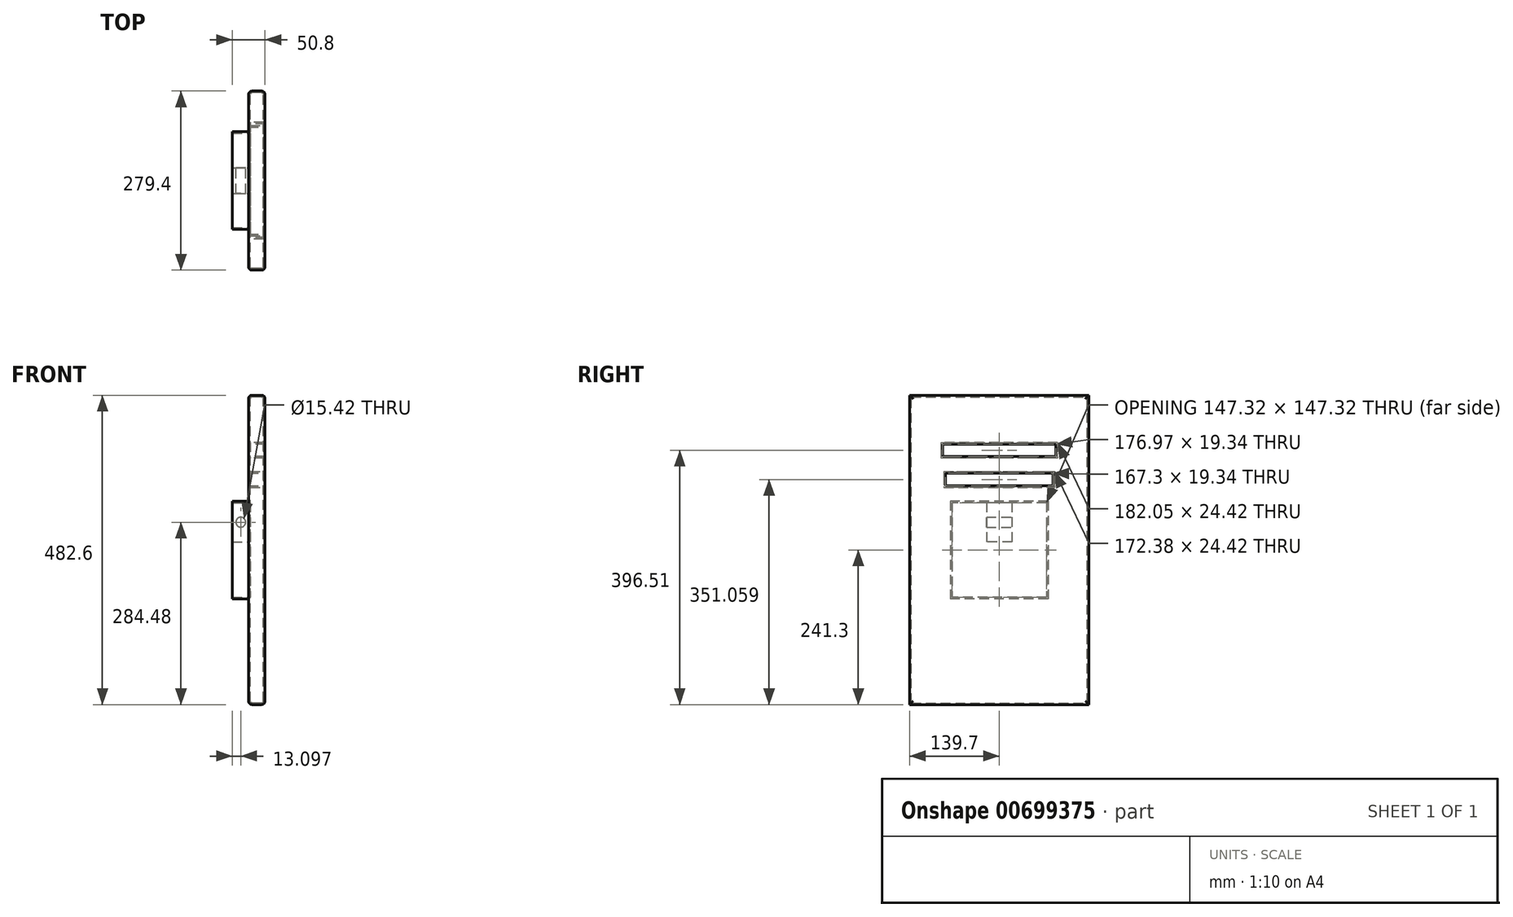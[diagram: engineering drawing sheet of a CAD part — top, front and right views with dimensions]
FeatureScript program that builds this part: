
annotation { "Feature Type Name" : "Feature", "Feature Type Description" : "" }
export const myFeature = defineFeature(function(context is Context, id is Id, definition is map)
    precondition{}
    {
        {
            var Q0;
            Q0=qCreatedBy(makeId("Right.planeOp"),FACE);
            var sketch = newSketch(context, id + "F0", { "sketchPlane" : qUnion([Q0])});
            skLineSegment(sketch, "E0.bottom", {"start": v(139.7, 241.3) * mm, "end": v(-139.7, 241.3) * mm});
            skLineSegment(sketch, "E0.top", {"start": v(139.7, -241.3) * mm, "end": v(-139.7, -241.3) * mm});
            skLineSegment(sketch, "E0.left", {"start": v(139.7, 241.3) * mm, "end": v(139.7, -241.3) * mm});
            skLineSegment(sketch, "E0.right", {"start": v(-139.7, 241.3) * mm, "end": v(-139.7, -241.3) * mm});
            skPoint(sketch, "E0.middle", {"position": v(0, 0) * mm});
            skSolve(sketch);
        }
        {
            var Q0;
            Q0 = qSketchRegion(id + "F0", true);
            var Q1;
            Q1=makeQuery(id+"F0.imprint","IMPRINT",FACE,{"disambiguationData":[TD([[makeQuery(id+"F0.imprint","IMPRINT",EDGE,{"derivedFrom":sQuery(id+"F0.wireOp",EDGE,"E0.bottom")}),1.0]])]});
            extrude(context, id + "F1", {"entities" : qUnion([Q0, Q1]), "depth" : 25.4 * mm, "offsetDistance" : 25.4 * mm});
        }
        {
            var Q0;
            Q0=makeQuery(id+"F1.opExtrude","CAP_FACE",FACE,{"disambiguationData":[OSD([sQuery(id+"F0.wireOp",EDGE,"E0.bottom"),sQuery(id+"F0.wireOp",EDGE,"E0.top"),sQuery(id+"F0.wireOp",EDGE,"E0.left"),sQuery(id+"F0.wireOp",EDGE,"E0.right")])],"isStart":true});
            fillet(context, id + "F2", {"entities" : qUnion([Q0]), "radius" : 5.08 * mm, "tangentPropagation" : true, "allowEdgeOverflow" : false});
        }
        {
            var Q0;
            Q0=makeQuery(id+"F1.opExtrude","CAP_FACE",FACE,{"disambiguationData":[OSD([sQuery(id+"F0.wireOp",EDGE,"E0.bottom"),sQuery(id+"F0.wireOp",EDGE,"E0.top"),sQuery(id+"F0.wireOp",EDGE,"E0.left"),sQuery(id+"F0.wireOp",EDGE,"E0.right")])],"isStart":false});
            fillet(context, id + "F3", {"entities" : qUnion([Q0]), "radius" : 5.08 * mm, "tangentPropagation" : true, "allowEdgeOverflow" : false});
        }
        {
            var Q0;
            Q0=makeQuery(id+"F1.opExtrude","CAP_FACE",FACE,{"disambiguationData":[OSD([sQuery(id+"F0.wireOp",EDGE,"E0.bottom"),sQuery(id+"F0.wireOp",EDGE,"E0.top"),sQuery(id+"F0.wireOp",EDGE,"E0.left"),sQuery(id+"F0.wireOp",EDGE,"E0.right")])],"isStart":true});
            var sketch = newSketch(context, id + "F4", { "sketchPlane" : qUnion([Q0])});
            skLineSegment(sketch, "E1.bottom", {"start": v(-88.48, 164.88) * mm, "end": v(88.48, 164.88) * mm});
            skLineSegment(sketch, "E1.top", {"start": v(-88.48, 145.54) * mm, "end": v(88.48, 145.54) * mm});
            skLineSegment(sketch, "E1.left", {"start": v(-88.48, 164.88) * mm, "end": v(-88.48, 145.54) * mm});
            skLineSegment(sketch, "E1.right", {"start": v(88.48, 164.88) * mm, "end": v(88.48, 145.54) * mm});
            skPoint(sketch, "E1.middle", {"position": v(0, 155.21) * mm});
            skSolve(sketch);
        }
        {
            var Q0;
            Q0=makeQuery(id+"F4.imprint","IMPRINT",FACE,{"disambiguationData":[TD([[makeQuery(id+"F4.imprint","IMPRINT",EDGE,{"derivedFrom":sQuery(id+"F4.wireOp",EDGE,"E1.bottom")}),-1.0]])]});
            extrude(context, id + "F5", {"entities" : qUnion([Q0]), "operationType" : NewBodyOperationType.REMOVE, "oppositeDirection" : true, "depth" : 25.4 * mm, "offsetDistance" : 25.4 * mm});
        }
        {
            var Q0;
            Q0=makeQuery(id+"F1.opExtrude","CAP_FACE",FACE,{"disambiguationData":[OSD([sQuery(id+"F0.wireOp",EDGE,"E0.bottom"),sQuery(id+"F0.wireOp",EDGE,"E0.top"),sQuery(id+"F0.wireOp",EDGE,"E0.left"),sQuery(id+"F0.wireOp",EDGE,"E0.right")])],"isStart":false});
            var sketch = newSketch(context, id + "F6", { "sketchPlane" : qUnion([Q0])});
            skLineSegment(sketch, "E2.bottom", {"start": v(-83.65, 119.43) * mm, "end": v(83.65, 119.43) * mm});
            skLineSegment(sketch, "E2.top", {"start": v(-83.65, 100.09) * mm, "end": v(83.65, 100.09) * mm});
            skLineSegment(sketch, "E2.left", {"start": v(-83.65, 119.43) * mm, "end": v(-83.65, 100.09) * mm});
            skLineSegment(sketch, "E2.right", {"start": v(83.65, 119.43) * mm, "end": v(83.65, 100.09) * mm});
            skPoint(sketch, "E2.middle", {"position": v(0, 109.76) * mm});
            skSolve(sketch);
        }
        {
            var Q0;
            Q0=makeQuery(id+"F6.imprint","IMPRINT",FACE,{"disambiguationData":[TD([[makeQuery(id+"F6.imprint","IMPRINT",EDGE,{"derivedFrom":sQuery(id+"F6.wireOp",EDGE,"E2.bottom")}),-1.0]])]});
            extrude(context, id + "F7", {"entities" : qUnion([Q0]), "operationType" : NewBodyOperationType.REMOVE, "oppositeDirection" : true, "depth" : 25.4 * mm, "offsetDistance" : 25.4 * mm});
        }
        {
            var Q0;
            Q0=makeQuery(id+"F1.opExtrude","CAP_FACE",FACE,{"disambiguationData":[OSD([sQuery(id+"F0.wireOp",EDGE,"E0.bottom"),sQuery(id+"F0.wireOp",EDGE,"E0.top"),sQuery(id+"F0.wireOp",EDGE,"E0.left"),sQuery(id+"F0.wireOp",EDGE,"E0.right")])],"isStart":true});
            var sketch = newSketch(context, id + "F8", { "sketchPlane" : qUnion([Q0])});
            skLineSegment(sketch, "E3.bottom", {"start": v(-76.2, 76.2) * mm, "end": v(76.2, 76.2) * mm});
            skLineSegment(sketch, "E3.top", {"start": v(-76.2, -76.2) * mm, "end": v(76.2, -76.2) * mm});
            skLineSegment(sketch, "E3.left", {"start": v(-76.2, 76.2) * mm, "end": v(-76.2, -76.2) * mm});
            skLineSegment(sketch, "E3.right", {"start": v(76.2, 76.2) * mm, "end": v(76.2, -76.2) * mm});
            skPoint(sketch, "E3.middle", {"position": v(0, 0) * mm});
            skSolve(sketch);
        }
        {
            var Q0;
            Q0=makeQuery(id+"F8.imprint","IMPRINT",FACE,{"disambiguationData":[TD([[makeQuery(id+"F8.imprint","IMPRINT",EDGE,{"derivedFrom":sQuery(id+"F8.wireOp",EDGE,"E3.bottom")}),-1.0]])]});
            extrude(context, id + "F9", {"entities" : qUnion([Q0]), "operationType" : NewBodyOperationType.ADD, "depth" : 25.4 * mm, "offsetDistance" : 25.4 * mm});
        }
        {
            var Q0;
            Q0=makeQuery(id+"F9.opExtrude","CAP_FACE",FACE,{"disambiguationData":[OSD([sQuery(id+"F8.wireOp",EDGE,"E3.bottom"),sQuery(id+"F8.wireOp",EDGE,"E3.top"),sQuery(id+"F8.wireOp",EDGE,"E3.left"),sQuery(id+"F8.wireOp",EDGE,"E3.right")])],"isStart":false});
            shell(context, id + "F10", {"entities" : qUnion([Q0]), "thickness" : 2.54 * mm});
        }
        {
            var Q0;
            Q0=makeQuery(id+"F1.opExtrude","CAP_FACE",FACE,{"disambiguationData":[OSD([sQuery(id+"F0.wireOp",EDGE,"E0.bottom"),sQuery(id+"F0.wireOp",EDGE,"E0.top"),sQuery(id+"F0.wireOp",EDGE,"E0.left"),sQuery(id+"F0.wireOp",EDGE,"E0.right")])],"isStart":true});
            var sketch = newSketch(context, id + "F11", { "sketchPlane" : qUnion([Q0])});
            skLineSegment(sketch, "E4.bottom", {"start": v(-19.82, 76.2) * mm, "end": v(19.82, 76.2) * mm});
            skLineSegment(sketch, "E4.top", {"start": v(-19.82, 12.7) * mm, "end": v(19.82, 12.7) * mm});
            skLineSegment(sketch, "E4.left", {"start": v(-19.82, 76.2) * mm, "end": v(-19.82, 12.7) * mm});
            skLineSegment(sketch, "E4.right", {"start": v(19.82, 76.2) * mm, "end": v(19.82, 12.7) * mm});
            skPoint(sketch, "E4.middle", {"position": v(0, 44.45) * mm});
            skSolve(sketch);
        }
        {
            var Q0;
            Q0=makeQuery(id+"F11.imprint","IMPRINT",FACE,{"disambiguationData":[TD([[makeQuery(id+"F11.imprint","IMPRINT",EDGE,{"derivedFrom":sQuery(id+"F11.wireOp",EDGE,"E4.bottom")}),-1.0]])]});
            extrude(context, id + "F12", {"entities" : qUnion([Q0]), "operationType" : NewBodyOperationType.ADD, "depth" : 25.4 * mm, "offsetDistance" : 25.4 * mm});
        }
        {
            var Q0;
            Q0=makeQuery(id+"F12.opExtrude","SWEPT_FACE",FACE,{"disambiguationData":[OSD([sQuery(id+"F11.wireOp",EDGE,"E4.left")])]});
            var sketch = newSketch(context, id + "F13", { "sketchPlane" : qUnion([Q0])});
            skCircle(sketch, "E5", {"center": v(12.3, 43.18) * mm, "radius": 7.71 * mm});
            skPoint(sketch, "E5.centerSnap0", {"position": v(0, 43.18) * mm});
            skSolve(sketch);
        }
        {
            var Q0;
            Q0=makeQuery(id+"F13.imprint","IMPRINT",FACE,{"disambiguationData":[TD([[makeQuery(id+"F13.imprint","IMPRINT",EDGE,{"derivedFrom":sQuery(id+"F13.wireOp",EDGE,"E5")}),1.0]])]});
            extrude(context, id + "F14", {"entities" : qUnion([Q0]), "operationType" : NewBodyOperationType.REMOVE, "oppositeDirection" : true, "depth" : 50.8 * mm, "offsetDistance" : 25.4 * mm});
        }
    });
